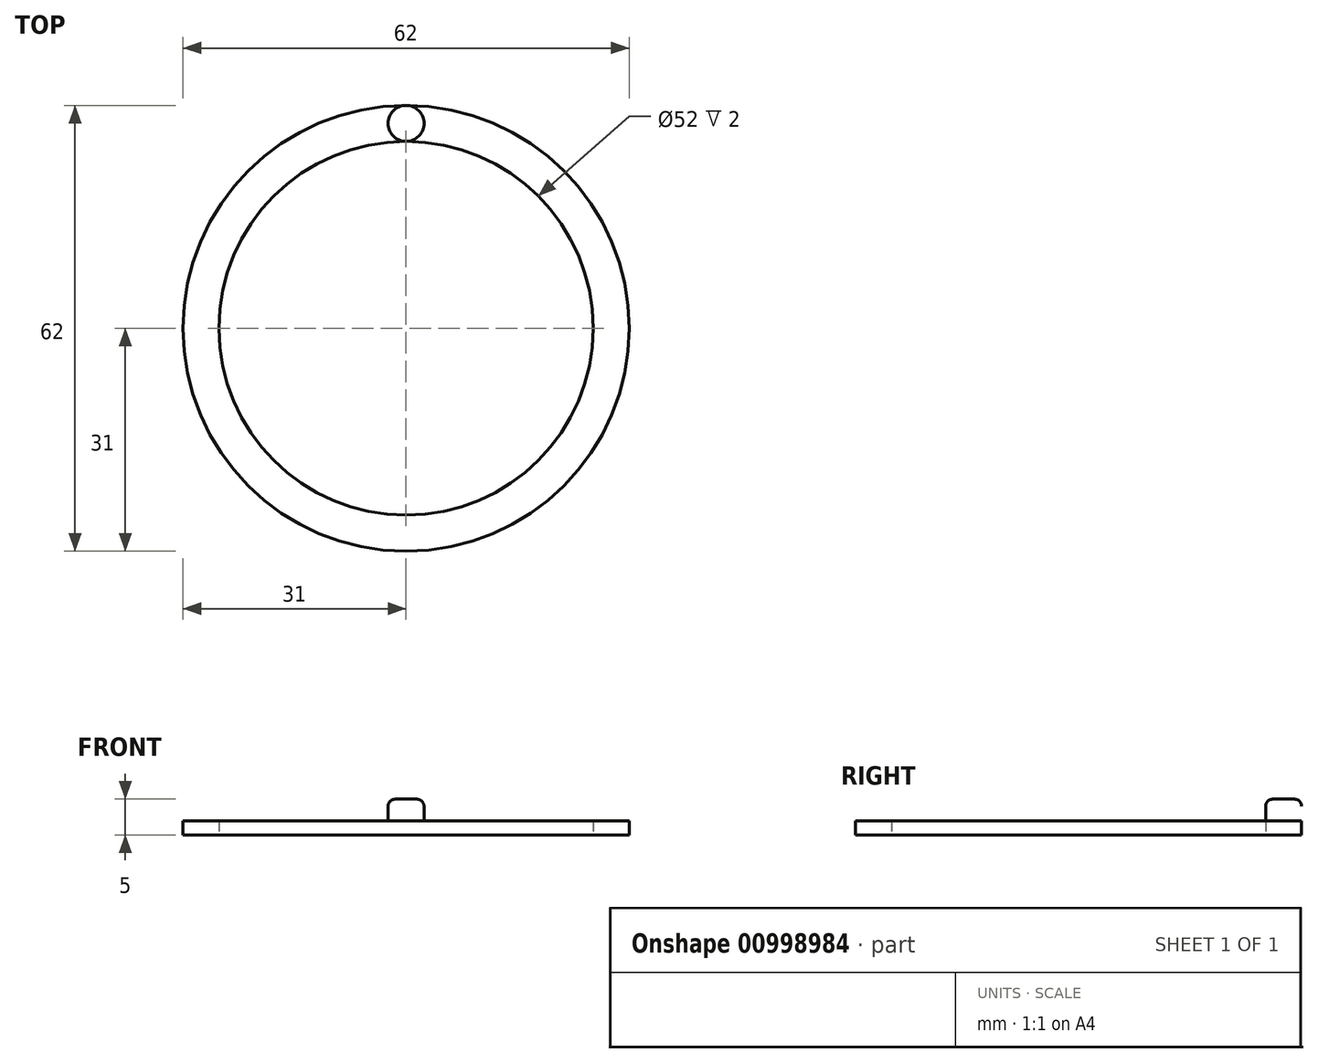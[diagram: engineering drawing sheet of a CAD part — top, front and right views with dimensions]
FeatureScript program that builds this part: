
annotation { "Feature Type Name" : "Feature", "Feature Type Description" : "" }
export const myFeature = defineFeature(function(context is Context, id is Id, definition is map)
    precondition{}
    {
        {
            var Q0;
            Q0=qCreatedBy(makeId("Top.planeOp"),FACE);
            var sketch = newSketch(context, id + "F0", { "sketchPlane" : qUnion([Q0])});
            skCircle(sketch, "E0", {"center": v(0, 0) * mm, "radius": 31 * mm});
            skCircle(sketch, "E1", {"center": v(0, 0) * mm, "radius": 26 * mm});
            skSolve(sketch);
        }
        {
            var Q0;
            Q0=makeQuery(id+"F0.imprint","IMPRINT",FACE,{"disambiguationData":[TD([[makeQuery(id+"F0.imprint","IMPRINT",EDGE,{"derivedFrom":sQuery(id+"F0.wireOp",EDGE,"E0")}),1.0]])]});
            extrude(context, id + "F1", {"entities" : qUnion([Q0]), "depth" : 2 * mm, "offsetDistance" : 25 * mm});
        }
        {
            var Q0;
            Q0=makeQuery(id+"F1.opExtrude","CAP_FACE",FACE,{"disambiguationData":[OSD([sQuery(id+"F0.wireOp",EDGE,"E0"),sQuery(id+"F0.wireOp",EDGE,"E1")])],"isStart":false});
            var sketch = newSketch(context, id + "F2", { "sketchPlane" : qUnion([Q0])});
            skLineSegment(sketch, "E2", {"start": v(0, 31) * mm, "end": v(0, 26) * mm, "construction": true});
            skCircle(sketch, "E3", {"center": v(0, 28.5) * mm, "radius": 2.5 * mm});
            skSolve(sketch);
        }
        {
            var Q0;
            Q0 = qSketchRegion(id + "F2", true);
            extrude(context, id + "F3", {"entities" : qUnion([Q0]), "operationType" : NewBodyOperationType.ADD, "depth" : 3 * mm, "offsetDistance" : 25 * mm});
        }
        {
            var Q0;
            Q0=makeQuery(id+"F3.boolean.opBoolean","SPLIT",EDGE,{"disambiguationData":[OD(0.0)],"derivedFrom":makeQuery(id+"F3.opExtrude","CAP_EDGE",EDGE,{"disambiguationData":[OSD([sQuery(id+"F2.wireOp",EDGE,"E3")])],"isStart":true})});
            var Q1;
            Q1=makeQuery(id+"F3.boolean.opBoolean","SPLIT",EDGE,{"disambiguationData":[OD(0.0)],"derivedFrom":makeQuery(id+"F3.opExtrude","CAP_EDGE",EDGE,{"disambiguationData":[OSD([sQuery(id+"F2.wireOp",EDGE,"8lG4bim0-H674-yoQb-quEU-0yL0QHVZMdGc")])],"isStart":true})});
            var Q2;
            Q2=makeQuery(id+"F3.boolean.opBoolean","SPLIT",EDGE,{"disambiguationData":[OD(0.0)],"derivedFrom":makeQuery(id+"F3.opExtrude","CAP_EDGE",EDGE,{"disambiguationData":[OSD([sQuery(id+"F2.wireOp",EDGE,"FeH3rE5n-BLOS-Li3Y-sZav-sdpjGpWOOnw1")])],"isStart":true})});
            var Q3;
            Q3=makeQuery(id+"F3.boolean.opBoolean","SPLIT",EDGE,{"disambiguationData":[OD(1.0)],"derivedFrom":makeQuery(id+"F3.opExtrude","CAP_EDGE",EDGE,{"disambiguationData":[OSD([sQuery(id+"F2.wireOp",EDGE,"4is09Ljp-Zow5-E4Aj-waDy-smTG0dwt7dS5")])],"isStart":true})});
            var Q4;
            Q4=makeQuery(id+"F3.opExtrude","CAP_EDGE",EDGE,{"disambiguationData":[OSD([sQuery(id+"F2.wireOp",EDGE,"FeH3rE5n-BLOS-Li3Y-sZav-sdpjGpWOOnw1")])],"isStart":false});
            var Q5;
            Q5=makeQuery(id+"F3.opExtrude","CAP_EDGE",EDGE,{"disambiguationData":[OSD([sQuery(id+"F2.wireOp",EDGE,"E3")])],"isStart":false});
            var Q6;
            Q6=makeQuery(id+"F3.opExtrude","CAP_EDGE",EDGE,{"disambiguationData":[OSD([sQuery(id+"F2.wireOp",EDGE,"8lG4bim0-H674-yoQb-quEU-0yL0QHVZMdGc")])],"isStart":false});
            var Q7;
            Q7=makeQuery(id+"F3.opExtrude","CAP_EDGE",EDGE,{"disambiguationData":[OSD([sQuery(id+"F2.wireOp",EDGE,"4is09Ljp-Zow5-E4Aj-waDy-smTG0dwt7dS5")])],"isStart":false});
            fillet(context, id + "F4", {"entities" : qUnion([Q0, Q1, Q2, Q3, Q4, Q5, Q6, Q7]), "radius" : 1 * mm, "tangentPropagation" : true, "allowEdgeOverflow" : false});
        }
    });
